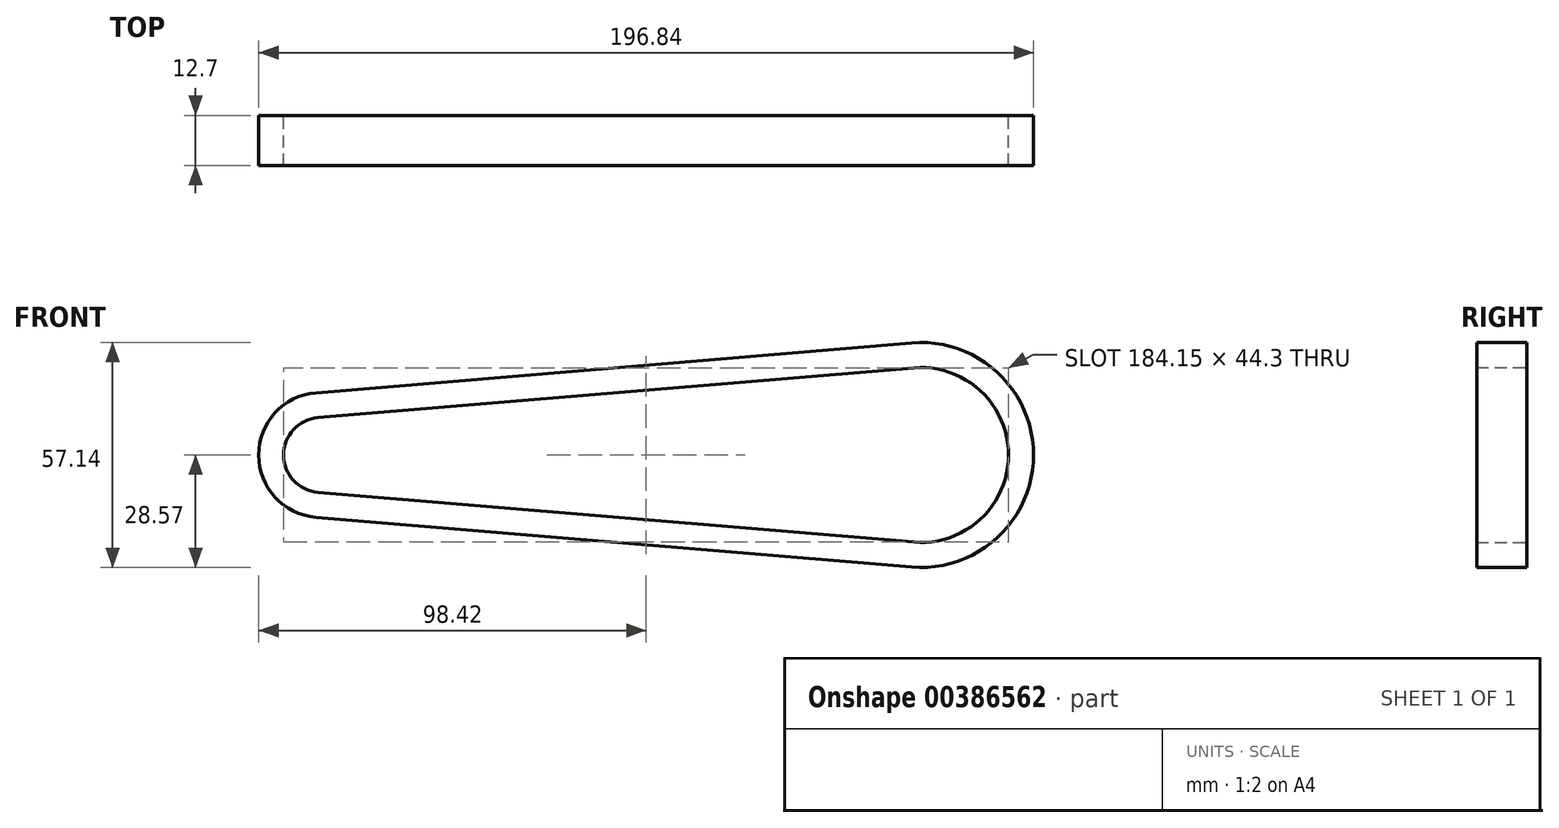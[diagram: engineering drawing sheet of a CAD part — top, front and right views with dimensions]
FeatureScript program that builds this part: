
annotation { "Feature Type Name" : "Feature", "Feature Type Description" : "" }
export const myFeature = defineFeature(function(context is Context, id is Id, definition is map)
    precondition{}
    {
        {
            var Q0;
            Q0=qCreatedBy(makeId("Front.planeOp"),FACE);
            var sketch = newSketch(context, id + "F0", { "sketchPlane" : qUnion([Q0])});
            skArc(sketch, "E0", {"start": v(-0.8, 9.5) * mm, "mid": v(-9.53, 0) * mm, "end": v(-0.8, -9.5) * mm});
            skArc(sketch, "E1", {"start": v(150.55, -22.15) * mm, "mid": v(174.62, 0) * mm, "end": v(150.55, 22.15) * mm});
            skLineSegment(sketch, "E2", {"start": v(-0.8, 9.5) * mm, "end": v(150.55, 22.15) * mm});
            skLineSegment(sketch, "E3", {"start": v(-0.8, -9.5) * mm, "end": v(150.55, -22.15) * mm});
            skSolve(sketch);
        }
        {
            var Q0;
            Q0=qCreatedBy(makeId("Front.planeOp"),FACE);
            var sketch = newSketch(context, id + "F1", { "sketchPlane" : qUnion([Q0])});
            skLineSegment(sketch, "E4.0", {"start": v(-1.32, 15.82) * mm, "end": v(150.02, 28.48) * mm});
            skArc(sketch, "E4.1", {"start": v(-1.32, 15.82) * mm, "mid": v(-15.87, 0) * mm, "end": v(-1.32, -15.82) * mm});
            skLineSegment(sketch, "E4.2", {"start": v(-1.32, -15.82) * mm, "end": v(150.02, -28.48) * mm});
            skArc(sketch, "E4.3", {"start": v(150.02, -28.48) * mm, "mid": v(180.97, 0) * mm, "end": v(150.02, 28.48) * mm});
            skSolve(sketch);
        }
        {
            var Q0;
            Q0=makeQuery(id+"F1.imprint","IMPRINT",FACE,{"disambiguationData":[TD([[makeQuery(id+"F1.imprint","IMPRINT",EDGE,{"derivedFrom":sQuery(id+"F1.wireOp",EDGE,"E4.0")}),-1.0]])]});
            extrude(context, id + "F2", {"entities" : qUnion([Q0]), "depth" : 12.7 * mm});
        }
        {
            var Q0;
            Q0 = qSketchRegion(id + "F0", true);
            extrude(context, id + "F3", {"entities" : qUnion([Q0]), "operationType" : NewBodyOperationType.REMOVE, "depth" : 25.4 * mm});
        }
    });
